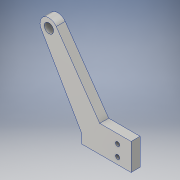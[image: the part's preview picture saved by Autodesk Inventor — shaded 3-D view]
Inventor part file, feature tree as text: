
AUTODESK INVENTOR PART (.ipt)
format: ipt  version: 2016 (Build 200138000, 138)  size: 125,952 bytes
history: native  units: in
note: dims shown in document units (in); Inventor stores cm internally (conversion verified against a paired STEP export)
features: thread x2, extrude x1, sketch x1
ambient origin geometry x8: Origin, YZ Plane, XZ Plane, XY Plane, X Axis, Y Axis, Z Axis, Center Point
bodies: Solid1 (feature_tree)
feature tree (4):
  extrude  "Extrusion1"  Depth=0.75in
  thread  "Thread1"  [1 undecoded]
  thread  "Thread2"  [1 undecoded]
  sketch  "Sketch1"  dims[d0=1.375in d1=0.75in d2=0.26in d3=150.0deg d4=1.59in d13=0.25in d14=0.0in d16=1.0in d17=0.25in d18=0.3125in d19=1.0in d20=0.1181in d21=0.1181in d22=0.5in d23=0.5in d24=0.5in d25=1.0in d26=0.0in d27=1.0in d28=0.0in]
note: 2 required parameter values undecoded (feature->parameter linkage not recoverable at this tier; creation-order binding heuristic only, values carry confidence <= 0.55)
